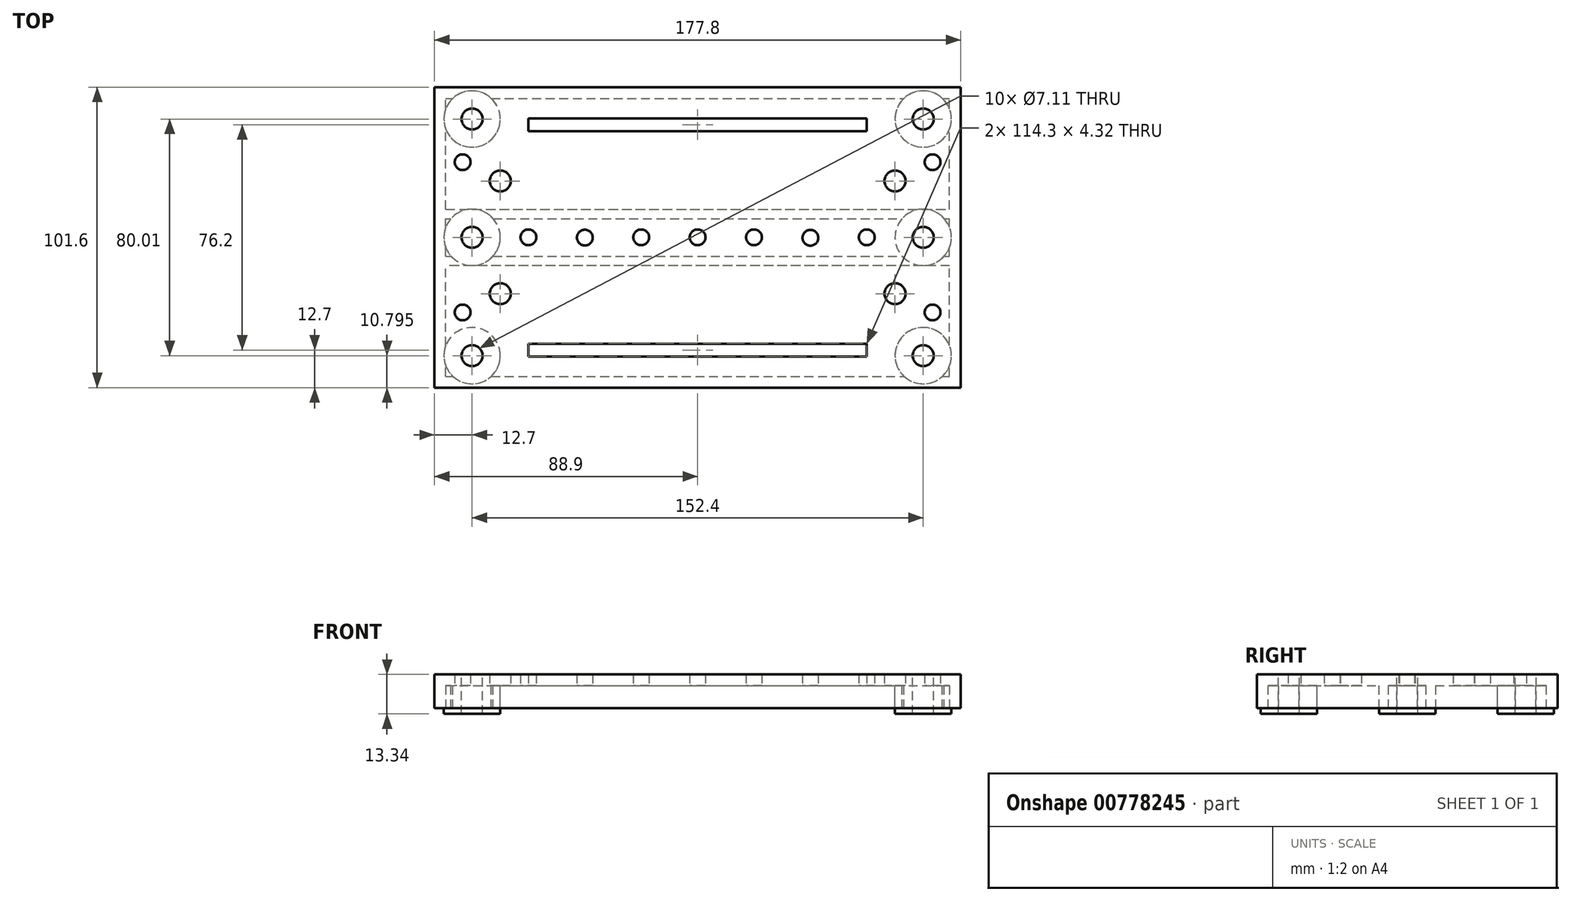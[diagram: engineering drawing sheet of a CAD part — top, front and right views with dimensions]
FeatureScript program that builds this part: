
annotation { "Feature Type Name" : "Feature", "Feature Type Description" : "" }
export const myFeature = defineFeature(function(context is Context, id is Id, definition is map)
    precondition{}
    {
        {
            var Q0;
            Q0=qCreatedBy(makeId("Top.planeOp"),FACE);
            var sketch = newSketch(context, id + "F0", { "sketchPlane" : qUnion([Q0])});
            skLineSegment(sketch, "E0.bottom", {"start": v(0, 0) * mm, "end": v(177.8, 0) * mm});
            skLineSegment(sketch, "E0.top", {"start": v(0, 101.6) * mm, "end": v(177.8, 101.6) * mm});
            skLineSegment(sketch, "E0.left", {"start": v(0, 0) * mm, "end": v(0, 101.6) * mm});
            skLineSegment(sketch, "E0.right", {"start": v(177.8, 0) * mm, "end": v(177.8, 101.6) * mm});
            skSolve(sketch);
        }
        {
            var Q0;
            Q0 = qSketchRegion(id + "F0", true);
            extrude(context, id + "F1", {"entities" : qUnion([Q0]), "depth" : 3.8 * mm, "offsetDistance" : 25.4 * mm});
        }
        {
            var Q0;
            Q0=qCreatedBy(makeId("Top.planeOp"),FACE);
            var sketch = newSketch(context, id + "F2", { "sketchPlane" : qUnion([Q0])});
            skCircle(sketch, "E1", {"center": v(22.22, 69.85) * mm, "radius": 3.56 * mm});
            skCircle(sketch, "E2", {"center": v(22.23, 31.75) * mm, "radius": 3.56 * mm});
            skCircle(sketch, "E3", {"center": v(155.58, 69.85) * mm, "radius": 3.56 * mm});
            skCircle(sketch, "E4", {"center": v(155.58, 31.75) * mm, "radius": 3.56 * mm});
            skSolve(sketch);
        }
        {
            var Q0;
            Q0=qCreatedBy(makeId("Top.planeOp"),FACE);
            var sketch = newSketch(context, id + "F3", { "sketchPlane" : qUnion([Q0])});
            skLineSegment(sketch, "E5", {"start": v(0, 88.9) * mm, "end": v(151.02, 88.9) * mm, "construction": true});
            skLineSegment(sketch, "E6", {"start": v(0, 12.7) * mm, "end": v(183.23, 12.7) * mm, "construction": true});
            skLineSegment(sketch, "E7.bottom", {"start": v(31.75, 91.06) * mm, "end": v(146.05, 91.06) * mm});
            skLineSegment(sketch, "E7.top", {"start": v(31.75, 86.74) * mm, "end": v(146.05, 86.74) * mm});
            skLineSegment(sketch, "E7.left", {"start": v(31.75, 91.06) * mm, "end": v(31.75, 86.74) * mm});
            skLineSegment(sketch, "E7.right", {"start": v(146.05, 91.06) * mm, "end": v(146.05, 86.74) * mm});
            skLineSegment(sketch, "E8.bottom", {"start": v(31.75, 14.86) * mm, "end": v(146.05, 14.86) * mm});
            skLineSegment(sketch, "E8.top", {"start": v(31.75, 10.54) * mm, "end": v(146.05, 10.54) * mm});
            skLineSegment(sketch, "E8.left", {"start": v(31.75, 14.86) * mm, "end": v(31.75, 10.54) * mm});
            skLineSegment(sketch, "E8.right", {"start": v(146.05, 14.86) * mm, "end": v(146.05, 10.54) * mm});
            skSolve(sketch);
        }
        {
            var Q0;
            Q0 = qSketchRegion(id + "F3", true);
            extrude(context, id + "F4", {"entities" : qUnion([Q0]), "operationType" : NewBodyOperationType.REMOVE, "endBound" : BoundingType.THROUGH_ALL, "depth" : 25.4 * mm, "offsetDistance" : 25.4 * mm});
        }
        {
            var Q0;
            Q0=qCreatedBy(makeId("Top.planeOp"),FACE);
            var sketch = newSketch(context, id + "F5", { "sketchPlane" : qUnion([Q0])});
            skCircle(sketch, "E9", {"center": v(12.7, 50.8) * mm, "radius": 9.53 * mm});
            skCircle(sketch, "E10", {"center": v(12.7, 90.8) * mm, "radius": 9.53 * mm});
            skCircle(sketch, "E11", {"center": v(12.7, 10.8) * mm, "radius": 9.53 * mm});
            skCircle(sketch, "E12", {"center": v(165.1, 90.8) * mm, "radius": 9.53 * mm});
            skCircle(sketch, "E13", {"center": v(165.1, 50.8) * mm, "radius": 9.53 * mm});
            skCircle(sketch, "E14", {"center": v(165.1, 10.8) * mm, "radius": 9.53 * mm});
            skSolve(sketch);
        }
        {
            var Q0;
            Q0 = qSketchRegion(id + "F5", true);
            extrude(context, id + "F6", {"entities" : qUnion([Q0]), "operationType" : NewBodyOperationType.ADD, "oppositeDirection" : true, "depth" : 9.52 * mm, "offsetDistance" : 25.4 * mm});
        }
        {
            var Q0;
            Q0=qCreatedBy(makeId("Top.planeOp"),FACE);
            var sketch = newSketch(context, id + "F7", { "sketchPlane" : qUnion([Q0])});
            skLineSegment(sketch, "E15.0", {"start": v(0, 41.27) * mm, "end": v(0, 44.45) * mm});
            skLineSegment(sketch, "E16.0", {"start": v(177.8, 41.28) * mm, "end": v(177.8, 44.45) * mm});
            skLineSegment(sketch, "E17", {"start": v(0, 44.45) * mm, "end": v(177.8, 44.45) * mm});
            skLineSegment(sketch, "E18", {"start": v(177.8, 41.28) * mm, "end": v(0, 41.27) * mm});
            skLineSegment(sketch, "E19", {"start": v(0, 57.15) * mm, "end": v(177.8, 57.15) * mm});
            skLineSegment(sketch, "E20", {"start": v(0, 60.33) * mm, "end": v(177.8, 60.33) * mm});
            skPoint(sketch, "E21.orphan", {"position": v(0, 0) * mm});
            skPoint(sketch, "E22.orphan", {"position": v(177.8, 0) * mm});
            skLineSegment(sketch, "E23.trimOffspring", {"start": v(177.8, 57.15) * mm, "end": v(177.8, 60.33) * mm});
            skLineSegment(sketch, "E24.trimOffspring", {"start": v(0, 57.15) * mm, "end": v(0, 60.33) * mm});
            skPoint(sketch, "E25.orphan", {"position": v(0, 101.6) * mm});
            skPoint(sketch, "E26.orphan", {"position": v(177.8, 101.6) * mm});
            skSolve(sketch);
        }
        {
            var Q0;
            Q0=qCreatedBy(makeId("Top.planeOp"),FACE);
            var sketch = newSketch(context, id + "F8", { "sketchPlane" : qUnion([Q0])});
            skLineSegment(sketch, "E27.0", {"start": v(0, 0) * mm, "end": v(177.8, 0) * mm});
            skLineSegment(sketch, "E28.0", {"start": v(0, 0) * mm, "end": v(0, 101.6) * mm});
            skLineSegment(sketch, "E29.0", {"start": v(0, 101.6) * mm, "end": v(177.8, 101.6) * mm});
            skLineSegment(sketch, "E30.0", {"start": v(177.8, 0) * mm, "end": v(177.8, 101.6) * mm});
            skLineSegment(sketch, "E31.bottom", {"start": v(3.81, 3.81) * mm, "end": v(173.99, 3.81) * mm});
            skLineSegment(sketch, "E31.top", {"start": v(3.8, 97.8) * mm, "end": v(173.99, 97.8) * mm});
            skLineSegment(sketch, "E31.left", {"start": v(3.81, 3.81) * mm, "end": v(3.8, 97.8) * mm});
            skLineSegment(sketch, "E31.right", {"start": v(173.99, 3.81) * mm, "end": v(173.99, 97.8) * mm});
            skSolve(sketch);
        }
        {
            var Q0;
            Q0 = qSketchRegion(id + "F8", true);
            extrude(context, id + "F9", {"entities" : qUnion([Q0]), "operationType" : NewBodyOperationType.ADD, "oppositeDirection" : true, "depth" : 7.62 * mm, "offsetDistance" : 25.4 * mm});
        }
        {
            var Q0;
            Q0=qCreatedBy(makeId("Top.planeOp"),FACE);
            var sketch = newSketch(context, id + "F10", { "sketchPlane" : qUnion([Q0])});
            skArc(sketch, "E32.0", {"start": v(3.8, 94.22) * mm, "mid": v(20.59, 85.46) * mm, "end": v(6.22, 97.8) * mm, "construction": true});
            skArc(sketch, "E33.0", {"start": v(3.8, 47.38) * mm, "mid": v(22.23, 50.8) * mm, "end": v(3.8, 54.22) * mm, "construction": true});
            skArc(sketch, "E34.0", {"start": v(6.22, 3.81) * mm, "mid": v(20.59, 16.14) * mm, "end": v(3.81, 7.38) * mm, "construction": true});
            skArc(sketch, "E35.0", {"start": v(171.58, 97.8) * mm, "mid": v(157.21, 85.46) * mm, "end": v(173.99, 94.22) * mm, "construction": true});
            skArc(sketch, "E36.0", {"start": v(173.99, 54.22) * mm, "mid": v(155.57, 50.8) * mm, "end": v(173.99, 47.38) * mm, "construction": true});
            skArc(sketch, "E37.0", {"start": v(173.99, 7.38) * mm, "mid": v(157.21, 16.14) * mm, "end": v(171.58, 3.8) * mm, "construction": true});
            skCircle(sketch, "E38", {"center": v(165.1, 50.8) * mm, "radius": 3.56 * mm});
            skCircle(sketch, "E39", {"center": v(165.1, 90.8) * mm, "radius": 3.56 * mm});
            skCircle(sketch, "E40", {"center": v(12.7, 10.8) * mm, "radius": 3.56 * mm});
            skCircle(sketch, "E41", {"center": v(12.7, 50.8) * mm, "radius": 3.56 * mm});
            skCircle(sketch, "E42", {"center": v(12.7, 90.8) * mm, "radius": 3.56 * mm});
            skCircle(sketch, "E43", {"center": v(165.1, 10.8) * mm, "radius": 3.56 * mm});
            skSolve(sketch);
        }
        {
            var Q0;
            Q0 = qSketchRegion(id + "F10", true);
            extrude(context, id + "F11", {"entities" : qUnion([Q0]), "operationType" : NewBodyOperationType.REMOVE, "endBound" : BoundingType.THROUGH_ALL, "oppositeDirection" : true, "depth" : 25.4 * mm, "offsetDistance" : 25.4 * mm, "hasSecondDirection" : true, "secondDirectionBound" : SecondDirectionBoundingType.THROUGH_ALL, "secondDirectionOppositeDirection" : false, "secondDirectionDepth" : 25.4 * mm});
        }
        {
            var Q0;
            Q0=qCreatedBy(makeId("Top.planeOp"),FACE);
            var sketch = newSketch(context, id + "F12", { "sketchPlane" : qUnion([Q0])});
            skCircle(sketch, "E44", {"center": v(31.75, 50.8) * mm, "radius": 2.67 * mm});
            skCircle(sketch, "E45", {"center": v(88.9, 50.8) * mm, "radius": 2.67 * mm});
            skCircle(sketch, "E46", {"center": v(146.05, 50.8) * mm, "radius": 2.67 * mm});
            skCircle(sketch, "E47", {"center": v(9.53, 25.4) * mm, "radius": 2.67 * mm});
            skCircle(sketch, "E48", {"center": v(9.53, 76.2) * mm, "radius": 2.67 * mm});
            skCircle(sketch, "E49", {"center": v(168.28, 25.4) * mm, "radius": 2.67 * mm});
            skCircle(sketch, "E50", {"center": v(168.28, 76.2) * mm, "radius": 2.67 * mm});
            skCircle(sketch, "E51", {"center": v(69.85, 50.8) * mm, "radius": 2.67 * mm});
            skCircle(sketch, "E52", {"center": v(107.95, 50.8) * mm, "radius": 2.67 * mm});
            skCircle(sketch, "E53", {"center": v(50.8, 50.7) * mm, "radius": 2.67 * mm});
            skCircle(sketch, "E54", {"center": v(127, 50.63) * mm, "radius": 2.67 * mm});
            skSolve(sketch);
        }
        {
            var Q0;
            Q0 = qSketchRegion(id + "F7", true);
            extrude(context, id + "F13", {"entities" : qUnion([Q0]), "operationType" : NewBodyOperationType.ADD, "oppositeDirection" : true, "depth" : 7.62 * mm, "offsetDistance" : 25.4 * mm});
        }
        {
            var Q0;
            Q0 = qSketchRegion(id + "F2", true);
            extrude(context, id + "F14", {"entities" : qUnion([Q0]), "operationType" : NewBodyOperationType.REMOVE, "endBound" : BoundingType.THROUGH_ALL, "depth" : 25.4 * mm, "offsetDistance" : 25.4 * mm});
        }
        {
            var Q0;
            Q0 = qSketchRegion(id + "F12", true);
            extrude(context, id + "F15", {"entities" : qUnion([Q0]), "operationType" : NewBodyOperationType.REMOVE, "endBound" : BoundingType.THROUGH_ALL, "depth" : 25.4 * mm, "offsetDistance" : 25.4 * mm});
        }
    });
